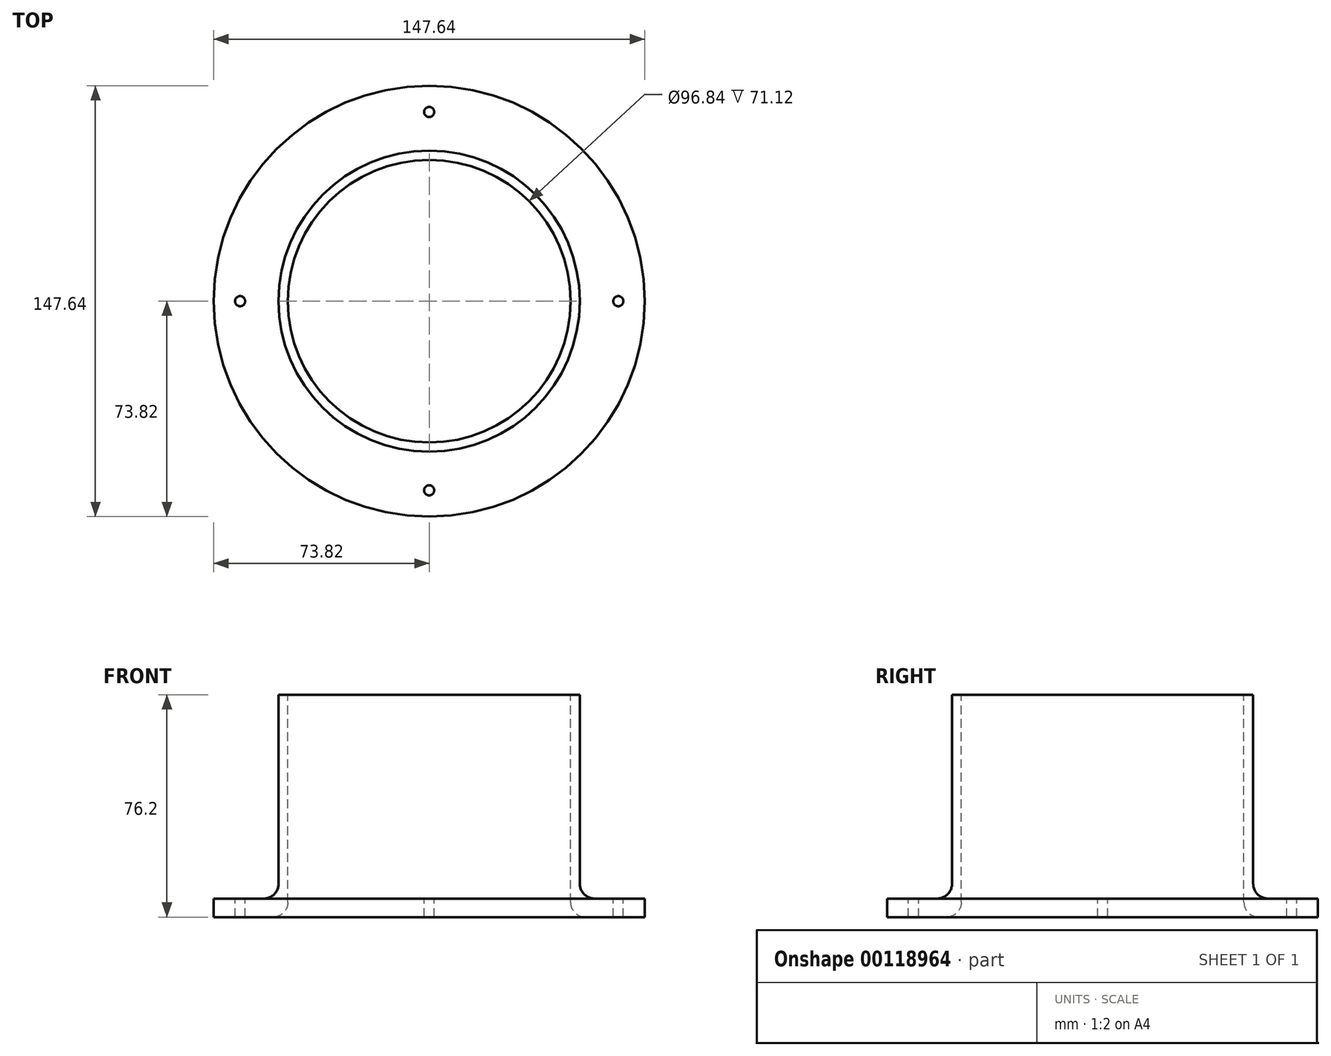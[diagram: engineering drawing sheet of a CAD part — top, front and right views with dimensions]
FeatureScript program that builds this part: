
annotation { "Feature Type Name" : "Feature", "Feature Type Description" : "" }
export const myFeature = defineFeature(function(context is Context, id is Id, definition is map)
    precondition{}
    {
        {
            var Q0;
            Q0=qCreatedBy(makeId("Top.planeOp"),FACE);
            var sketch = newSketch(context, id + "F0", { "sketchPlane" : qUnion([Q0])});
            skCircle(sketch, "E0", {"center": v(0, 0) * mm, "radius": 51.6 * mm});
            skSolve(sketch);
        }
        {
            var Q0;
            Q0 = qSketchRegion(id + "F0", true);
            extrude(context, id + "F1", {"entities" : qUnion([Q0]), "depth" : 76.2 * mm});
        }
        {
            var Q0;
            Q0=qCreatedBy(makeId("Top.planeOp"),FACE);
            var sketch = newSketch(context, id + "F2", { "sketchPlane" : qUnion([Q0])});
            skCircle(sketch, "E1.0", {"center": v(0, 0) * mm, "radius": 73.82 * mm});
            skSolve(sketch);
        }
        {
            var Q0;
            Q0=makeQuery(id+"F2.imprint","IMPRINT",FACE,{"disambiguationData":[TD([[makeQuery(id+"F2.imprint","IMPRINT",EDGE,{"derivedFrom":sQuery(id+"F2.wireOp",EDGE,"E1.0")}),1.0]])]});
            extrude(context, id + "F3", {"entities" : qUnion([Q0]), "operationType" : NewBodyOperationType.ADD, "depth" : 6.35 * mm});
        }
        {
            var Q0;
            Q0=makeQuery(id+"F1.opExtrude","CAP_FACE",FACE,{"disambiguationData":[OSD([sQuery(id+"F0.wireOp",EDGE,"E0")])],"isStart":false});
            var sketch = newSketch(context, id + "F4", { "sketchPlane" : qUnion([Q0])});
            skCircle(sketch, "E2.0", {"center": v(0, 0) * mm, "radius": 48.42 * mm});
            skSolve(sketch);
        }
        {
            var Q0;
            Q0=makeQuery(id+"F4.imprint","IMPRINT",FACE,{"disambiguationData":[TD([[makeQuery(id+"F4.imprint","IMPRINT",EDGE,{"derivedFrom":sQuery(id+"F4.wireOp",EDGE,"E2.0")}),1.0]])]});
            extrude(context, id + "F5", {"entities" : qUnion([Q0]), "operationType" : NewBodyOperationType.REMOVE, "endBound" : BoundingType.THROUGH_ALL, "oppositeDirection" : true, "depth" : 25.4 * mm});
        }
        {
            var Q0;
            Q0=makeQuery(id+"F3.boolean.opBoolean","INTERSECT",EDGE,{"derivedFrom":[makeQuery(id+"F1.opExtrude","SWEPT_FACE",FACE,{"disambiguationData":[OSD([sQuery(id+"F0.wireOp",EDGE,"E0")])]}),makeQuery(id+"F3.opExtrude","CAP_FACE",FACE,{"disambiguationData":[OSD([sQuery(id+"F2.wireOp",EDGE,"E1.0")])],"isStart":false})]});
            fillet(context, id + "F6", {"entities" : qUnion([Q0]), "radius" : 5.08 * mm, "tangentPropagation" : true, "allowEdgeOverflow" : false});
        }
        {
            var Q0;
            Q0=makeQuery(id+"F5.boolean.opBoolean","INTERSECT",EDGE,{"derivedFrom":[makeQuery(id+"F3.boolean.opBoolean","MERGE",FACE,{"derivedFrom":[makeQuery(id+"F1.opExtrude","CAP_FACE",FACE,{"disambiguationData":[OSD([sQuery(id+"F0.wireOp",EDGE,"E0")])],"isStart":true}),makeQuery(id+"F3.opExtrude","CAP_FACE",FACE,{"disambiguationData":[OSD([sQuery(id+"F2.wireOp",EDGE,"E1.0")])],"isStart":true})]}),makeQuery(id+"F5.opExtrude","SWEPT_FACE",FACE,{"disambiguationData":[OSD([sQuery(id+"F4.wireOp",EDGE,"E2.0")])]})]});
            fillet(context, id + "F7", {"entities" : qUnion([Q0]), "radius" : 5.08 * mm, "tangentPropagation" : true, "allowEdgeOverflow" : false});
        }
        {
            var Q0;
            Q0=makeQuery(id+"F3.opExtrude","CAP_FACE",FACE,{"disambiguationData":[OSD([sQuery(id+"F2.wireOp",EDGE,"E1.0")])],"isStart":false});
            var sketch = newSketch(context, id + "F8", { "sketchPlane" : qUnion([Q0])});
            skCircle(sketch, "E3", {"center": v(64.8, 0) * mm, "radius": 1.73 * mm});
            skCircle(sketch, "E4.1.0", {"center": v(0, 64.8) * mm, "radius": 1.73 * mm});
            skCircle(sketch, "E4.2.0", {"center": v(-64.8, 0) * mm, "radius": 1.73 * mm});
            skCircle(sketch, "E4.3.0", {"center": v(0, -64.8) * mm, "radius": 1.73 * mm});
            skPoint(sketch, "E4.center", {"position": v(0, 0) * mm});
            skSolve(sketch);
        }
        {
            var Q0;
            Q0 = qSketchRegion(id + "F8", true);
            extrude(context, id + "F9", {"entities" : qUnion([Q0]), "operationType" : NewBodyOperationType.REMOVE, "endBound" : BoundingType.THROUGH_ALL, "oppositeDirection" : true, "depth" : 25.4 * mm});
        }
    });
